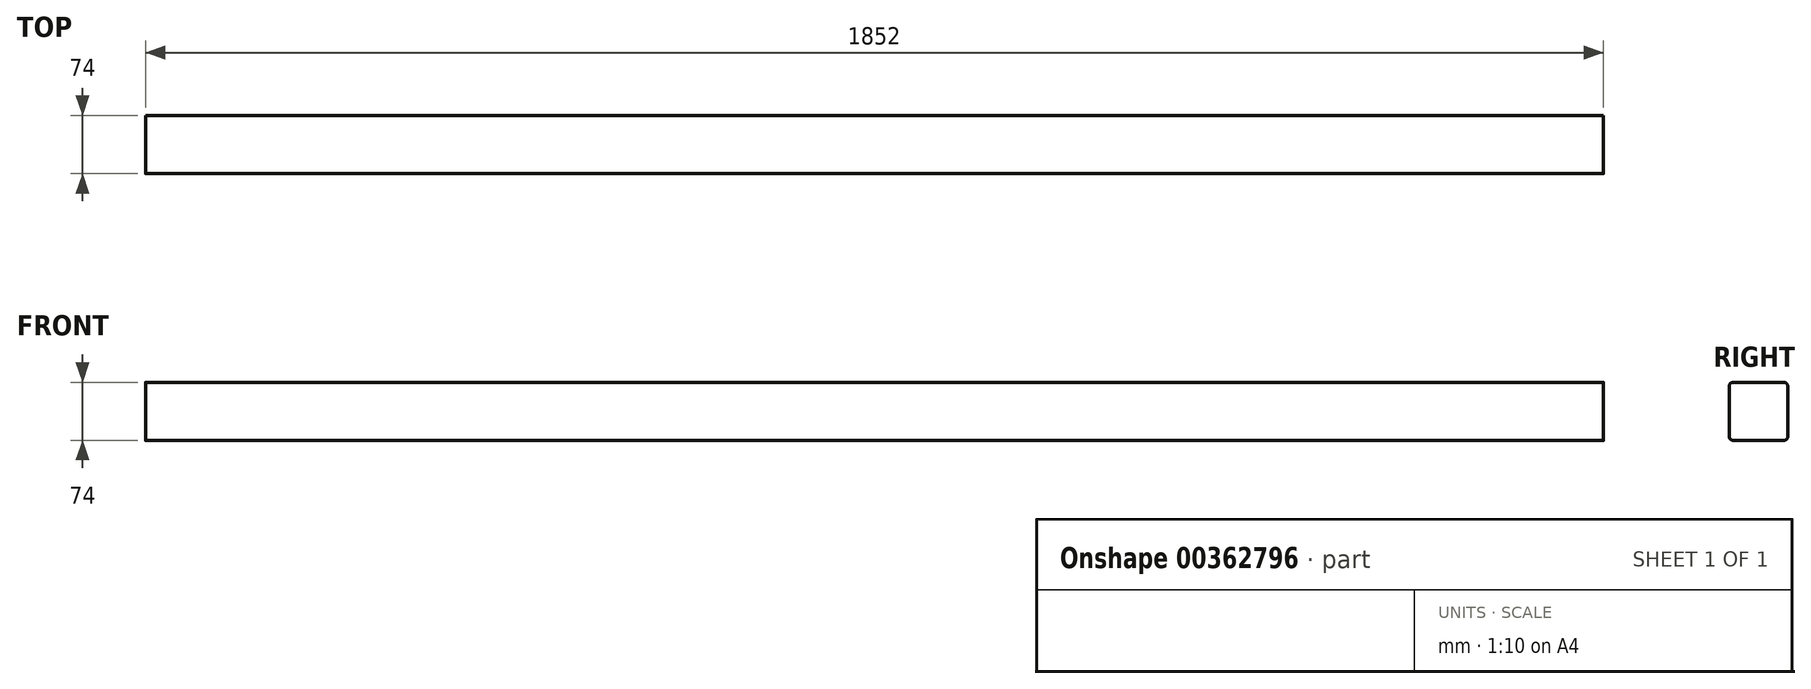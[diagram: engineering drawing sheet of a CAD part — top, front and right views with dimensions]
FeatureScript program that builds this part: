
annotation { "Feature Type Name" : "Feature", "Feature Type Description" : "" }
export const myFeature = defineFeature(function(context is Context, id is Id, definition is map)
    precondition{}
    {
        {
            var Q0;
            Q0=qCreatedBy(makeId("Right.planeOp"),FACE);
            var sketch = newSketch(context, id + "F0", { "sketchPlane" : qUnion([Q0])});
            skLineSegment(sketch, "E0.bottom", {"start": v(37, 37) * mm, "end": v(-37, 37) * mm});
            skLineSegment(sketch, "E0.top", {"start": v(37, -37) * mm, "end": v(-37, -37) * mm});
            skLineSegment(sketch, "E0.left", {"start": v(37, 37) * mm, "end": v(37, -37) * mm});
            skLineSegment(sketch, "E0.right", {"start": v(-37, 37) * mm, "end": v(-37, -37) * mm});
            skPoint(sketch, "E0.middle", {"position": v(0, 0) * mm});
            skSolve(sketch);
        }
        {
            var Q0;
            Q0=makeQuery(id+"F0.imprint","IMPRINT",FACE,{"disambiguationData":[TD([[makeQuery(id+"F0.imprint","IMPRINT",EDGE,{"derivedFrom":sQuery(id+"F0.wireOp",EDGE,"E0.bottom")}),1.0]])]});
            extrude(context, id + "F1", {"entities" : qUnion([Q0]), "depth" : (2000 - 74 * 2) * mm});
        }
        {
            var Q0;
            Q0=makeQuery(id+"F1.opExtrude","SWEPT_EDGE",EDGE,{"disambiguationData":[OSD([sQuery(id+"F0.wireOp",EDGE,"E0.bottom"),sQuery(id+"F0.wireOp",EDGE,"E0.left")])]});
            var Q1;
            Q1=makeQuery(id+"F1.opExtrude","SWEPT_EDGE",EDGE,{"disambiguationData":[OSD([sQuery(id+"F0.wireOp",EDGE,"E0.bottom"),sQuery(id+"F0.wireOp",EDGE,"E0.right")])]});
            var Q2;
            Q2=makeQuery(id+"F1.opExtrude","SWEPT_EDGE",EDGE,{"disambiguationData":[OSD([sQuery(id+"F0.wireOp",EDGE,"E0.top"),sQuery(id+"F0.wireOp",EDGE,"E0.right")])]});
            var Q3;
            Q3=makeQuery(id+"F1.opExtrude","SWEPT_EDGE",EDGE,{"disambiguationData":[OSD([sQuery(id+"F0.wireOp",EDGE,"E0.top"),sQuery(id+"F0.wireOp",EDGE,"E0.left")])]});
            fillet(context, id + "F2", {"entities" : qUnion([Q0, Q1, Q2, Q3]), "radius" : 5 * mm, "tangentPropagation" : true, "allowEdgeOverflow" : false});
        }
    });
